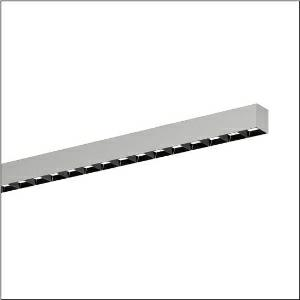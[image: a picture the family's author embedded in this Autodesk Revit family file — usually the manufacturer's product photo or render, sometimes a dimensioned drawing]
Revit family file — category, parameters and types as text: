
# Revit family: silica_r__21_51mx24dc3asb_5aec
name_source: partatom
category: Lighting Fixtures
units: mm (PartAtom-declared; Revit-internal decimal feet)

## family parameters
Cut with Voids When Loaded = No
Host = Face
Light Source = No
Part Type = Normal
Room Calculation Point = No
Round Connector Dimension = Use Diameter
Shared = No

## types (1)
- --- (1 x LED, 10800 lm, 79 W, 3000K)
    Apparent Load = 79 VA
    CIE Flux Codes = 74 94 99 100 100
    Color Rendering = 80
    Color Temperature = 3000K
    Default Elevation = 1800 mm
    Description = Silica® 21, office luminaire, primary light control with darklight reflector, of PMMA, black, CAT 2 (L<= 3000cd/m²), light emission: direct distribution, primary light characteristic: asymmetric, installation type: surface-mounted, LED, rated luminous flux: 10.800lm, luminous efficacy: 137lm/W, light colour: 830, colour temperature: 3000K, control gear: DALI 2, with terminal, 3+2-pole, max. 2.5mm², mains connection: 220..240V, AC, 50/60Hz, rated input power: 79W, luminaire housing, of aluminium, metallic grey (RAL 9006), length: 3.004mm, width: 53mm, height: 53mm, protection rating (complete): IP20, insulation class (complete): insulation class I (protective earthing), certification: CE, permissible operating ambient temperature: 0..+35°C, standard: EN 50419, packaging unit: 1 piece
    Height = 53 mm
    Lamp = 1 x LED
    Lamp Light Flux = 10800 lm
    Lamp Power = 79 W
    Lamp count = 1
    Length = 3004 mm
    Luminous efficacy = 137 lm/W
    Manufacturer = Siteco
    ModVariant = No
    Model = 51MX24DC3ASB
    Mounting Place = Ceiling
    Mounting Type = Surface mounted
    Number of Poles = 1
    OnlyDefault = Yes
    Power Factor = 1
    Product Name = Silica® 21
    Product group = office luminaire | ceiling mounted
    ProductGroupID = 302
    Protection Class = Protection class I
    Protection Degree = IP 20
    RLX_Detail_Level = 1
    RLX_Emergency_Light_Flux = 0 lm
    RLX_Emergency_Type = 0
    RLX_Emergency_Type_DB = No
    RlxData = <blob elided: 63441 chars, md5=07eeb215>
    Socket = socket
    Standby Power = 0 W
    System Light Flux = 10800 lm
    System Power = 79 W
    Type Comments = factory setting: luminous flux: 100 % | dim-lin: 254 | 448 mA
    Type Image = l_1335929.jpg
    URL = http://relux.com
    VarID = @adj_122572
    Voltage = 0 V
    Weight = 0.00 kg
    Width = 53 mm

## geometry (parser evidence)
native form markers: Blend x4, Sweep x10
no freeform markers — native parametric forms only
